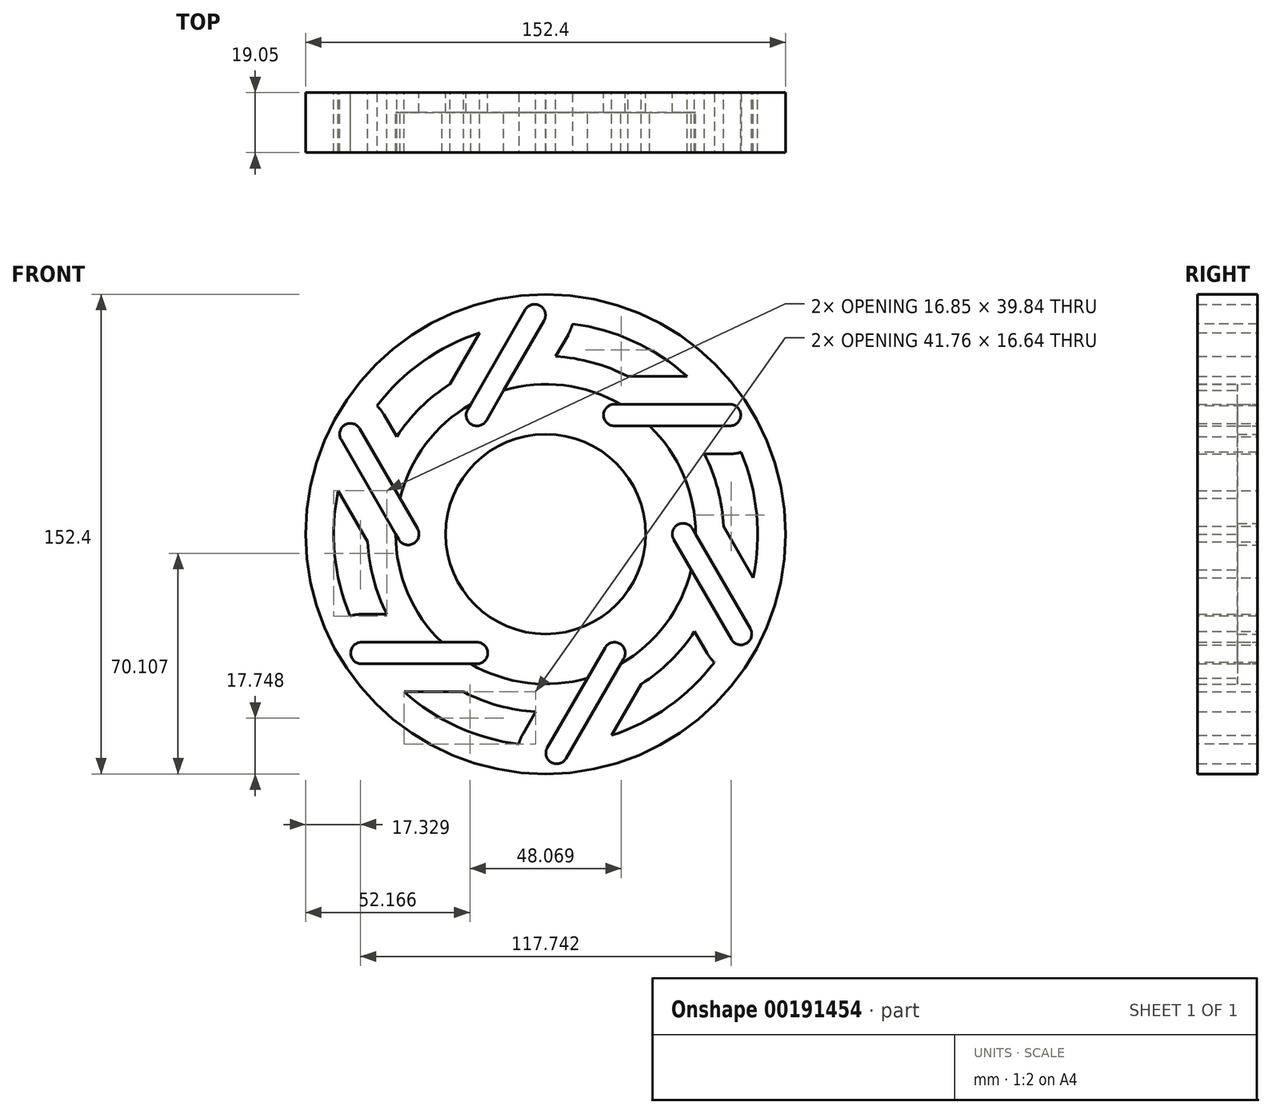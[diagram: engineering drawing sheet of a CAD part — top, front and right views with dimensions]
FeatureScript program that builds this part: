
annotation { "Feature Type Name" : "Feature", "Feature Type Description" : "" }
export const myFeature = defineFeature(function(context is Context, id is Id, definition is map)
    precondition{}
    {
        {
            var Q0;
            Q0=qCreatedBy(makeId("Front.planeOp"),FACE);
            var sketch = newSketch(context, id + "F0", { "sketchPlane" : qUnion([Q0])});
            skPoint(sketch, "E0", {"position": v(0, 0) * mm});
            skCircle(sketch, "E1", {"center": v(0, 0) * mm, "radius": 31.75 * mm});
            skPoint(sketch, "E2", {"position": v(-31.75, 0) * mm});
            skPoint(sketch, "E3", {"position": v(31.75, 0) * mm});
            skPoint(sketch, "E4", {"position": v(-39.69, 0) * mm});
            skPoint(sketch, "E5", {"position": v(39.69, 0) * mm});
            skPoint(sketch, "E6", {"position": v(-15.88, -27.5) * mm});
            skPoint(sketch, "E7", {"position": v(15.88, -27.5) * mm});
            skPoint(sketch, "E8", {"position": v(15.88, 27.5) * mm});
            skPoint(sketch, "E9", {"position": v(-15.88, 27.5) * mm});
            skPoint(sketch, "E10", {"position": v(-19.84, 34.37) * mm});
            skPoint(sketch, "E11", {"position": v(19.84, 34.37) * mm});
            skPoint(sketch, "E12", {"position": v(19.84, -34.37) * mm});
            skPoint(sketch, "E13", {"position": v(-19.84, -34.37) * mm});
            skPoint(sketch, "E14", {"position": v(-47.63, 0) * mm});
            skPoint(sketch, "E15", {"position": v(47.63, 0) * mm});
            skLineSegment(sketch, "E16", {"start": v(-40.68, 1.72) * mm, "end": v(-46.25, 11.36) * mm});
            skLineSegment(sketch, "E17", {"start": v(-18.85, 36.09) * mm, "end": v(-13.28, 45.74) * mm});
            skLineSegment(sketch, "E18", {"start": v(21.83, 34.37) * mm, "end": v(32.97, 34.37) * mm});
            skLineSegment(sketch, "E19", {"start": v(40.68, -1.72) * mm, "end": v(46.25, -11.36) * mm});
            skLineSegment(sketch, "E20", {"start": v(18.85, -36.09) * mm, "end": v(13.28, -45.74) * mm});
            skLineSegment(sketch, "E21", {"start": v(-21.83, -34.37) * mm, "end": v(-32.97, -34.37) * mm});
            skPoint(sketch, "E22", {"position": v(-43.66, 0) * mm});
            skPoint(sketch, "E23", {"position": v(-21.83, 37.8) * mm});
            skPoint(sketch, "E24", {"position": v(-21.83, -37.8) * mm});
            skPoint(sketch, "E25", {"position": v(21.83, -37.8) * mm});
            skPoint(sketch, "E26", {"position": v(43.66, 0) * mm});
            skArc(sketch, "E27", {"start": v(-21.83, -41.24) * mm, "mid": v(-18.4, -37.8) * mm, "end": v(-21.83, -34.37) * mm});
            skArc(sketch, "E28", {"start": v(24.8, -39.53) * mm, "mid": v(23.55, -34.83) * mm, "end": v(18.85, -36.09) * mm});
            skArc(sketch, "E29", {"start": v(46.63, 1.72) * mm, "mid": v(41.94, 2.98) * mm, "end": v(40.68, -1.72) * mm});
            skArc(sketch, "E30", {"start": v(-24.8, 39.53) * mm, "mid": v(-23.55, 34.83) * mm, "end": v(-18.85, 36.09) * mm});
            skArc(sketch, "E31", {"start": v(-46.63, -1.72) * mm, "mid": v(-41.94, -2.98) * mm, "end": v(-40.68, 1.72) * mm});
            skPoint(sketch, "E32", {"position": v(21.83, 37.8) * mm});
            skArc(sketch, "E33", {"start": v(21.83, 41.24) * mm, "mid": v(18.4, 37.8) * mm, "end": v(21.83, 34.37) * mm});
            skPoint(sketch, "E34", {"position": v(40.68, -1.72) * mm});
            skPoint(sketch, "E35", {"position": v(46.63, 1.72) * mm});
            skPoint(sketch, "E36", {"position": v(21.83, 34.37) * mm});
            skPoint(sketch, "E37", {"position": v(-18.85, 36.09) * mm});
            skPoint(sketch, "E38", {"position": v(-40.68, 1.72) * mm});
            skPoint(sketch, "E39", {"position": v(-21.83, -34.37) * mm});
            skPoint(sketch, "E40", {"position": v(18.85, -36.09) * mm});
            skPoint(sketch, "E41", {"position": v(24.8, -39.53) * mm});
            skPoint(sketch, "E42", {"position": v(-21.83, -41.24) * mm});
            skPoint(sketch, "E43", {"position": v(-46.63, -1.72) * mm});
            skPoint(sketch, "E44", {"position": v(-24.8, 39.53) * mm});
            skPoint(sketch, "E45", {"position": v(21.83, 41.24) * mm});
            skLineSegment(sketch, "E46", {"start": v(21.83, 34.37) * mm, "end": v(58.49, 34.37) * mm});
            skLineSegment(sketch, "E47", {"start": v(-18.85, 36.09) * mm, "end": v(-0.52, 67.84) * mm});
            skLineSegment(sketch, "E48", {"start": v(-40.68, 1.72) * mm, "end": v(-59.01, 33.47) * mm});
            skLineSegment(sketch, "E49", {"start": v(-21.83, -34.37) * mm, "end": v(-58.49, -34.37) * mm});
            skLineSegment(sketch, "E50", {"start": v(18.85, -36.09) * mm, "end": v(0.52, -67.84) * mm});
            skLineSegment(sketch, "E51", {"start": v(40.68, -1.72) * mm, "end": v(59.01, -33.47) * mm});
            skPoint(sketch, "E52", {"position": v(-59.01, 33.47) * mm});
            skPoint(sketch, "E53", {"position": v(-0.52, 67.84) * mm});
            skPoint(sketch, "E54", {"position": v(58.49, 34.37) * mm});
            skPoint(sketch, "E55", {"position": v(59.01, -33.47) * mm});
            skPoint(sketch, "E56", {"position": v(0.52, -67.84) * mm});
            skPoint(sketch, "E57", {"position": v(-58.49, -34.37) * mm});
            skPoint(sketch, "E58", {"position": v(29.77, -46.4) * mm});
            skLineSegment(sketch, "E59", {"start": v(46.63, 1.72) * mm, "end": v(64.96, -30.03) * mm});
            skLineSegment(sketch, "E60", {"start": v(21.83, 41.24) * mm, "end": v(58.49, 41.24) * mm});
            skLineSegment(sketch, "E61", {"start": v(-24.8, 39.53) * mm, "end": v(-6.47, 71.28) * mm});
            skLineSegment(sketch, "E62", {"start": v(-46.63, -1.72) * mm, "end": v(-64.96, 30.03) * mm});
            skLineSegment(sketch, "E63", {"start": v(-21.83, -41.24) * mm, "end": v(-58.49, -41.24) * mm});
            skLineSegment(sketch, "E64", {"start": v(24.8, -39.53) * mm, "end": v(6.47, -71.28) * mm});
            skPoint(sketch, "E65", {"position": v(-64.96, 30.03) * mm});
            skPoint(sketch, "E66", {"position": v(-58.49, -41.24) * mm});
            skPoint(sketch, "E67", {"position": v(6.47, -71.28) * mm});
            skPoint(sketch, "E68", {"position": v(64.96, -30.03) * mm});
            skPoint(sketch, "E69", {"position": v(58.49, 41.24) * mm});
            skPoint(sketch, "E70", {"position": v(-6.47, 71.28) * mm});
            skArc(sketch, "E71", {"start": v(46.25, 11.36) * mm, "mid": v(41.24, 23.81) * mm, "end": v(32.97, 34.37) * mm});
            skArc(sketch, "E72.trimOffspring", {"start": v(32.97, -34.37) * mm, "mid": v(41.24, -23.81) * mm, "end": v(46.25, -11.36) * mm});
            skArc(sketch, "E73.trimOffspring", {"start": v(-13.28, -45.74) * mm, "mid": v(0, -47.63) * mm, "end": v(13.28, -45.74) * mm});
            skArc(sketch, "E74.trimOffspring", {"start": v(-46.25, -11.36) * mm, "mid": v(-41.24, -23.81) * mm, "end": v(-32.97, -34.37) * mm});
            skArc(sketch, "E75", {"start": v(23.81, 41.24) * mm, "mid": v(5.72, 47.28) * mm, "end": v(-13.28, 45.74) * mm});
            skArc(sketch, "E76.trimOffspring", {"start": v(47.63, 0) * mm, "mid": v(47.28, 5.72) * mm, "end": v(46.25, 11.36) * mm});
            skArc(sketch, "E77.trimOffspring", {"start": v(23.81, -41.24) * mm, "mid": v(28.6, -38.08) * mm, "end": v(32.97, -34.37) * mm});
            skArc(sketch, "E78.trimOffspring", {"start": v(-23.81, -41.24) * mm, "mid": v(-18.68, -43.8) * mm, "end": v(-13.28, -45.74) * mm});
            skArc(sketch, "E79.trimOffspring", {"start": v(-23.81, 41.24) * mm, "mid": v(-38.08, 28.6) * mm, "end": v(-46.25, 11.36) * mm});
            skArc(sketch, "E80.trimOffspring", {"start": v(-47.63, 0) * mm, "mid": v(-47.28, -5.72) * mm, "end": v(-46.25, -11.36) * mm});
            skPoint(sketch, "E81", {"position": v(-61.99, 31.75) * mm});
            skPoint(sketch, "E82", {"position": v(-58.49, -37.8) * mm});
            skPoint(sketch, "E83", {"position": v(3.5, -69.56) * mm});
            skPoint(sketch, "E84", {"position": v(61.99, -31.75) * mm});
            skPoint(sketch, "E85", {"position": v(58.49, 37.8) * mm});
            skPoint(sketch, "E86", {"position": v(-3.5, 69.56) * mm});
            skArc(sketch, "E87", {"start": v(-0.52, 67.84) * mm, "mid": v(-1.78, 72.53) * mm, "end": v(-6.47, 71.28) * mm});
            skArc(sketch, "E88", {"start": v(-59.01, 33.47) * mm, "mid": v(-63.7, 34.73) * mm, "end": v(-64.96, 30.03) * mm});
            skArc(sketch, "E89", {"start": v(58.49, 34.37) * mm, "mid": v(61.93, 37.8) * mm, "end": v(58.49, 41.24) * mm});
            skArc(sketch, "E90", {"start": v(59.01, -33.47) * mm, "mid": v(63.7, -34.73) * mm, "end": v(64.96, -30.03) * mm});
            skArc(sketch, "E91", {"start": v(0.52, -67.84) * mm, "mid": v(1.78, -72.53) * mm, "end": v(6.47, -71.28) * mm});
            skArc(sketch, "E92", {"start": v(-58.49, -34.37) * mm, "mid": v(-61.93, -37.8) * mm, "end": v(-58.49, -41.24) * mm});
            skCircle(sketch, "E93", {"center": v(0, 0) * mm, "radius": 76.2 * mm});
            skSolve(sketch);
        }
        {
            var Q0;
            Q0=makeQuery(id+"F0.imprint","IMPRINT",FACE,{"disambiguationData":[TD([[makeQuery(id+"F0.imprint","IMPRINT",EDGE,{"derivedFrom":sQuery(id+"F0.wireOp",EDGE,"E1")}),-1.0]])]});
            extrude(context, id + "F1", {"entities" : qUnion([Q0]), "depth" : 6.35 * mm});
        }
        {
            var Q0;
            {var subQ26=sQuery(id+"F0.wireOp",EDGE,"E71");Q0=makeQuery(id+"F0.imprint","IMPRINT",FACE,{"disambiguationData":[TD([[makeQuery(id+"F0.imprint","IMPRINT",EDGE,{"derivedFrom":subQ26}),-1.0]])]});}
            extrude(context, id + "F2", {"entities" : qUnion([Q0]), "operationType" : NewBodyOperationType.ADD, "depth" : 19.05 * mm});
        }
        {
            var Q0;
            Q0=makeQuery(id+"F2.opExtrude","CAP_FACE",FACE,{"disambiguationData":[OSD([sQuery(id+"F0.wireOp",EDGE,"E46"),sQuery(id+"F0.wireOp",EDGE,"E47"),sQuery(id+"F0.wireOp",EDGE,"E48"),sQuery(id+"F0.wireOp",EDGE,"E49"),sQuery(id+"F0.wireOp",EDGE,"E50"),sQuery(id+"F0.wireOp",EDGE,"E51"),sQuery(id+"F0.wireOp",EDGE,"E59"),sQuery(id+"F0.wireOp",EDGE,"E60"),sQuery(id+"F0.wireOp",EDGE,"E61"),sQuery(id+"F0.wireOp",EDGE,"E62"),sQuery(id+"F0.wireOp",EDGE,"E63"),sQuery(id+"F0.wireOp",EDGE,"E64"),sQuery(id+"F0.wireOp",EDGE,"E71"),sQuery(id+"F0.wireOp",EDGE,"E72.trimOffspring"),sQuery(id+"F0.wireOp",EDGE,"E73.trimOffspring"),sQuery(id+"F0.wireOp",EDGE,"E74.trimOffspring"),sQuery(id+"F0.wireOp",EDGE,"E75"),sQuery(id+"F0.wireOp",EDGE,"E76.trimOffspring"),sQuery(id+"F0.wireOp",EDGE,"E77.trimOffspring"),sQuery(id+"F0.wireOp",EDGE,"E78.trimOffspring"),sQuery(id+"F0.wireOp",EDGE,"E79.trimOffspring"),sQuery(id+"F0.wireOp",EDGE,"E80.trimOffspring"),sQuery(id+"F0.wireOp",EDGE,"E87"),sQuery(id+"F0.wireOp",EDGE,"E88"),sQuery(id+"F0.wireOp",EDGE,"E89"),sQuery(id+"F0.wireOp",EDGE,"E90"),sQuery(id+"F0.wireOp",EDGE,"E91"),sQuery(id+"F0.wireOp",EDGE,"E92"),sQuery(id+"F0.wireOp",EDGE,"E93")])],"isStart":false});
            var Q1;
            {var subQ0=sQuery(id+"F0.wireOp",EDGE,"E80.trimOffspring");var subQ1=sQuery(id+"F0.wireOp",EDGE,"E79.trimOffspring");var subQ2=sQuery(id+"F0.wireOp",EDGE,"E78.trimOffspring");var subQ3=sQuery(id+"F0.wireOp",EDGE,"E77.trimOffspring");var subQ4=sQuery(id+"F0.wireOp",EDGE,"E76.trimOffspring");var subQ5=sQuery(id+"F0.wireOp",EDGE,"E75");var subQ6=sQuery(id+"F0.wireOp",EDGE,"E74.trimOffspring");var subQ7=sQuery(id+"F0.wireOp",EDGE,"E73.trimOffspring");var subQ8=sQuery(id+"F0.wireOp",EDGE,"E72.trimOffspring");var subQ9=sQuery(id+"F0.wireOp",EDGE,"E71");var subQ10=sQuery(id+"F0.wireOp",EDGE,"E64");var subQ11=sQuery(id+"F0.wireOp",EDGE,"E63");var subQ12=sQuery(id+"F0.wireOp",EDGE,"E62");var subQ13=sQuery(id+"F0.wireOp",EDGE,"E61");var subQ14=sQuery(id+"F0.wireOp",EDGE,"E60");var subQ15=sQuery(id+"F0.wireOp",EDGE,"E59");var subQ16=sQuery(id+"F0.wireOp",EDGE,"E51");var subQ17=sQuery(id+"F0.wireOp",EDGE,"E50");var subQ18=sQuery(id+"F0.wireOp",EDGE,"E49");var subQ19=sQuery(id+"F0.wireOp",EDGE,"E48");var subQ20=sQuery(id+"F0.wireOp",EDGE,"E47");var subQ21=sQuery(id+"F0.wireOp",EDGE,"E46");Q1=makeQuery(id+"F2.boolean.opBoolean","MERGE",FACE,{"derivedFrom":[makeQuery(id+"F1.opExtrude","CAP_FACE",FACE,{"disambiguationData":[OSD([sQuery(id+"F0.wireOp",EDGE,"E1"),sQuery(id+"F0.wireOp",EDGE,"E27"),sQuery(id+"F0.wireOp",EDGE,"E28"),sQuery(id+"F0.wireOp",EDGE,"E29"),sQuery(id+"F0.wireOp",EDGE,"E30"),sQuery(id+"F0.wireOp",EDGE,"E31"),sQuery(id+"F0.wireOp",EDGE,"E33"),subQ21,subQ20,subQ19,subQ18,subQ17,subQ16,subQ15,subQ14,subQ13,subQ12,subQ11,subQ10,subQ9,subQ8,subQ7,subQ6,subQ5,subQ4,subQ3,subQ2,subQ1,subQ0])],"isStart":true}),makeQuery(id+"F2.opExtrude","CAP_FACE",FACE,{"disambiguationData":[OSD([subQ21,subQ20,subQ19,subQ18,subQ17,subQ16,subQ15,subQ14,subQ13,subQ12,subQ11,subQ10,subQ9,subQ8,subQ7,subQ6,subQ5,subQ4,subQ3,subQ2,subQ1,subQ0,sQuery(id+"F0.wireOp",EDGE,"E87"),sQuery(id+"F0.wireOp",EDGE,"E88"),sQuery(id+"F0.wireOp",EDGE,"E89"),sQuery(id+"F0.wireOp",EDGE,"E90"),sQuery(id+"F0.wireOp",EDGE,"E91"),sQuery(id+"F0.wireOp",EDGE,"E92"),sQuery(id+"F0.wireOp",EDGE,"E93")])],"isStart":true})]});}
            shell(context, id + "F3", {"entities" : qUnion([Q0, Q1]), "thickness" : 8.9 * mm});
        }
    });
